FCSTD DOCUMENT  (FreeCAD 1.0R39319 (Git))
Label: ASSEMBLY-VSN1-LEFT
License: All rights reserved
LicenseURL: https://en.wikipedia.org/wiki/All_rights_reserved
objects: App::DocumentObjectGroup×3, App::Link×3, Sketcher::SketchObject×2, PartDesign::CoordinateSystem×1, App::FeaturePython×1, App::Part×1, PartDesign::Body×1
note: 6 computed .brp shape members not serialized (recipe doc carries the construction recipe); baked Part::Feature solids carry a one-line shape summary decoded from their .brp
EXTERNAL_REF file=ASSEMBLY-CANVAS.FCStd obj=LCS_Origin
EXTERNAL_REF file=ASSEMBLY-CANVAS.FCStd obj=Assembly
EXTERNAL_REF file=ASSEMBLY-VSN1-PCB-LEFT.FCStd obj=LCS_Origin
EXTERNAL_REF file=ASSEMBLY-VSN1-PCB-LEFT.FCStd obj=Assembly
EXTERNAL_REF file=ASSEMBLY-VSN1-FRONTPANEL-LEFT.FCStd obj=LCS_Origin
EXTERNAL_REF file=ASSEMBLY-VSN1-FRONTPANEL-LEFT.FCStd obj=Assembly

FEATURE [App::DocumentObjectGroup] Parts
FEATURE [PartDesign::CoordinateSystem] LCS_Origin
  AttacherType = Attacher::AttachEngine3D
  AttachmentSupport = -> [X_Axis]
  MapMode = 2
FEATURE [App::DocumentObjectGroup] Constraints
FEATURE [App::FeaturePython] Variables  # WARN: FeaturePython — macro-defined, semantics opaque (R4)
  Type = App::PropertyContainer
FEATURE [App::DocumentObjectGroup] Configurations
FEATURE [App::Link] ASSEMBLY_CANVAS_Assembly4  label="ASSEMBLY_CANVAS"
  AttachedBy = #LCS_Origin
  AttachedTo = Parent Assembly#LCS_Origin
  LinkedObject = -> <external ASSEMBLY-CANVAS.FCStd>#Assembly
  SolverId = Asm4EE
  expr: Placement = LCS_Origin.Placement * AttachmentOffset * ASSEMBLY_CANVAS#LCS_Origin.Placement ^ -1
FEATURE [App::Link] ASSEMBLY_VSN1_PCB_LEFT
  AttachedBy = #LCS_Origin
  AttachedTo = ASSEMBLY_CANVAS_Assembly4#LCS_Origin
  AttachmentOffset = pos=(0,0,-9.6) rot=(0,0,1;0rad)
  LinkPlacement = pos=(0,0,-9.6) rot=(0,0,1;0rad)
  LinkedObject = -> <external ASSEMBLY-VSN1-PCB-LEFT.FCStd>#Assembly
  Placement = pos=(0,0,-9.6) rot=(0,0,1;0rad)
  SolverId = Asm4EE
  expr: Placement = ASSEMBLY_CANVAS_Assembly4.Placement * ASSEMBLY_CANVAS#LCS_Origin.Placement * AttachmentOffset * ASSEMBLY_VSN1_PCB_LEFT#LCS_Origin.Placement ^ -1
FEATURE [App::Link] ASSEMBLY_VSN1_FRONTPANEL_LEFT
  AttachedBy = #LCS_Origin
  AttachedTo = ASSEMBLY_CANVAS_Assembly4#LCS_Origin
  AttachmentOffset = pos=(0,0,0.59) rot=(0,0,1;0rad)
  LinkPlacement = pos=(0,0,0.59) rot=(0,0,1;0rad)
  LinkedObject = -> <external ASSEMBLY-VSN1-FRONTPANEL-LEFT.FCStd>#Assembly
  Placement = pos=(0,0,0.59) rot=(0,0,1;0rad)
  SolverId = Asm4EE
  expr: Placement = ASSEMBLY_CANVAS_Assembly4.Placement * ASSEMBLY_CANVAS#LCS_Origin.Placement * AttachmentOffset * ASSEMBLY_VSN1_FRONTPANEL_LEFT#LCS_Origin.Placement ^ -1
FEATURE [Sketcher::SketchObject] Sketch_1
  ArcFitTolerance = 1e-06
  AttachmentSupport = -> [XZ_Plane]
  FullyConstrained = true
  MakeInternals = false
  MapMode = 5
  Placement = pos=(0,0,0) rot=(1,0,0;1.5708rad)
FEATURE [App::Part] Assembly
  AssemblyType = Part::Link
  Group = -> [LCS_Origin,Constraints,Variables,Configurations,ASSEMBLY_CANVAS_Assembly4,ASSEMBLY_VSN1_PCB_LEFT,ASSEMBLY_VSN1_FRONTPANEL_LEFT,Sketch_1]
  Origin = -> Origin
  Type = Assembly
FEATURE [Sketcher::SketchObject] Sketch
  ArcFitTolerance = 1e-06
  AttachmentOffset = pos=(0,0,26.67) rot=(0,0,1;0rad)
  AttachmentSupport = -> [XZ_Plane001]
  FullyConstrained = true
  MakeInternals = false
  MapMode = 5
  Placement = pos=(0,-26.67,5.9e-15) rot=(1,0,0;1.5708rad)
FEATURE [PartDesign::Body] Body
  AllowCompound = false
  Group = -> [Sketch]
  Origin = -> Origin001

RESOLVED EXTERNAL PARTS (link-assembly join: the EXTERNAL_REF files above that resolve inside this repo's crawl, each included once):
---- part ASSEMBLY-CANVAS.FCStd = doc fcstd_c2d832810578 ----
FCSTD DOCUMENT  (FreeCAD 1.0R39319 (Git))
Label: ASSEMBLY-CANVAS
License: All rights reserved
LicenseURL: https://en.wikipedia.org/wiki/All_rights_reserved
objects: App::Link×9, Part::FeaturePython×7, App::DocumentObjectGroup×3, PartDesign::CoordinateSystem×2, App::FeaturePython×1, Sketcher::SketchObject×1, App::Part×1
note: 11 computed .brp shape members not serialized (recipe doc carries the construction recipe); baked Part::Feature solids carry a one-line shape summary decoded from their .brp
EXTERNAL_REF file=../Design/PLASTIC-CANVAS/PLASTIC-CANVAS.FCStd obj=LCS_Origin
EXTERNAL_REF file=../Design/PLASTIC-CANVAS/PLASTIC-CANVAS.FCStd obj=Body002
EXTERNAL_REF file=../Design/PLASTIC-CANVAS/PLASTIC-CANVAS.FCStd obj=CircleAxis_1
EXTERNAL_REF file=../Design/RUBBER-FOOT/RUBBER-FOOT.FCStd obj=CircleAxis_2
EXTERNAL_REF file=../Design/RUBBER-FOOT/RUBBER-FOOT.FCStd obj=Body
EXTERNAL_REF file=../Design/INSERT-M1.6x2.5x3/INSERT-M1.6x2.5x3.FCStd obj=CircleAxis_1
EXTERNAL_REF file=../Design/PLASTIC-CANVAS/PLASTIC-CANVAS.FCStd obj=CircleAxis_3
EXTERNAL_REF file=../Design/INSERT-M1.6x2.5x3/INSERT-M1.6x2.5x3.FCStd obj=Body
EXTERNAL_REF file=../Design/INSERT-M1.6x2.5x4/INSERT-M1.6x2.5x4.FCStd obj=Plane_1
EXTERNAL_REF file=../Design/PLASTIC-CANVAS/PLASTIC-CANVAS.FCStd obj=CircleAxis_4
EXTERNAL_REF file=../Design/INSERT-M1.6x2.5x4/INSERT-M1.6x2.5x4.FCStd obj=Body
EXTERNAL_REF file=../Design/MAGNET-D3x14/MAGNET-D3x14.FCStd obj=LCS_1
EXTERNAL_REF file=../Design/PLASTIC-CANVAS/PLASTIC-CANVAS.FCStd obj=LCS_3
EXTERNAL_REF file=../Design/MAGNET-D3x14/MAGNET-D3x14.FCStd obj=Body001
EXTERNAL_REF file=../Design/PLASTIC-CANVAS/PLASTIC-CANVAS.FCStd obj=LCS_4
EXTERNAL_REF file=../Design/MAGNET-SQ3/MAGNET-SQ3.FCStd obj=Axis_2
EXTERNAL_REF file=../Design/PLASTIC-CANVAS/PLASTIC-CANVAS.FCStd obj=Axis_2
EXTERNAL_REF file=../Design/MAGNET-SQ3/MAGNET-SQ3.FCStd obj=Body002
EXTERNAL_REF file=PCBAs/PCBA-INTERFACE.FCStd obj=CircleAxis_1
EXTERNAL_REF file=../Design/PLASTIC-CANVAS/PLASTIC-CANVAS.FCStd obj=Axis_3
EXTERNAL_REF file=PCBAs/PCBA-INTERFACE.FCStd obj=PCBA_INTERFACE_3D_1
EXTERNAL_REF file=../Design/PLASTIC-CANVAS/PLASTIC-CANVAS.FCStd obj=LCS_5
EXTERNAL_REF file=../Design/PLASTIC-MAPMODE/PLASTIC-MAPMODE.FCStd obj=LCS_1
EXTERNAL_REF file=../Design/PLASTIC-MAPMODE/PLASTIC-MAPMODE.FCStd obj=Body

FEATURE [App::DocumentObjectGroup] Parts
FEATURE [PartDesign::CoordinateSystem] LCS_Origin
  AttacherType = Attacher::AttachEngine3D
  AttachmentSupport = -> [X_Axis]
  MapMode = 2
FEATURE [App::DocumentObjectGroup] Constraints
FEATURE [App::FeaturePython] Variables  # WARN: FeaturePython — macro-defined, semantics opaque (R4)
  Type = App::PropertyContainer
FEATURE [App::DocumentObjectGroup] Configurations
FEATURE [App::Link] PLASTIC_CANVAS  label="PLASTIC-CANVAS"
  AttachedBy = #LCS_Origin
  AttachedTo = Parent Assembly#LCS_Origin
  LinkedObject = -> <external ../Design/PLASTIC-CANVAS/PLASTIC-CANVAS.FCStd>#Body002
  SolverId = Asm4EE
  expr: Placement = LCS_Origin.Placement * AttachmentOffset * PLASTIC_CANVAS#LCS_Origin.Placement ^ -1
FEATURE [App::Link] RUBBER_FOOT  label="RUBBER-FOOT"
  AttachedBy = #CircleAxis_2
  AttachedTo = PLASTIC_CANVAS#CircleAxis_1
  LinkPlacement = pos=(-33.85,38,-16) rot=(0,0,1;0rad)
  LinkedObject = -> <external ../Design/RUBBER-FOOT/RUBBER-FOOT.FCStd>#Body
  Placement = pos=(-33.85,38,-16) rot=(0,0,1;0rad)
  SolverId = Asm4EE
  expr: Placement = PLASTIC_CANVAS.Placement * PLASTIC_CANVAS#CircleAxis_1.Placement * AttachmentOffset * RUBBER_FOOT#CircleAxis_2.Placement ^ -1
FEATURE [Part::FeaturePython] Circular_RUBBER_FOOT  label="Circular_RUBBER-FOOT"  # Draft array (typed FeaturePython)
  AngleStep = 90
  ArrayType = Circular Array
  Axis = -> LCS_Origin [Z]
  Count = 4
  Index = 1
  PlacementList = 4 placements: [(-33.85,38,-16),(-38,-33.85,-16),(33.85,-38,-16),(38,33.85,-16)]
  Placer = pos=(0,0,0) rot=(0,0,1;4.71239rad)
  ScaleList = (4) [(1,1,1),(1,1,1),(1,1,1),(1,1,1)]
  Scaler = 1
  ShowElement = false
  SourceObject = -> RUBBER_FOOT
  expr: .Placer.Rotation.Angle = AngleStep * Index
  expr: AngleStep = 360 / Count
FEATURE [App::Link] INSERT_M1_6x2_5x3  label="INSERT-M1.6x2.5x3"
  AttachedBy = #CircleAxis_1
  AttachedTo = PLASTIC_CANVAS#CircleAxis_3
  AttachmentOffset = pos=(0,0,0) rot=(1,0,0;3.14159rad)
  LinkPlacement = pos=(-26.67,26.67,-14) rot=(1,0,0;3.14159rad)
  LinkedObject = -> <external ../Design/INSERT-M1.6x2.5x3/INSERT-M1.6x2.5x3.FCStd>#Body
  Placement = pos=(-26.67,26.67,-14) rot=(1,0,0;3.14159rad)
  SolverId = Asm4EE
  expr: Placement = PLASTIC_CANVAS.Placement * PLASTIC_CANVAS#CircleAxis_3.Placement * AttachmentOffset * INSERT_M1_6x2_5x3#CircleAxis_1.Placement ^ -1
FEATURE [Part::FeaturePython] Circular_INSERT_M1_6x2_5x3  label="Circular_INSERT-M1.6x2.5x3"  # Draft array (typed FeaturePython)
  AngleStep = 90
  ArrayType = Circular Array
  Axis = -> LCS_Origin [Z]
  Count = 4
  Index = 1
  PlacementList = 4 placements: [(-26.67,26.67,-14),(-26.67,-26.67,-14),(26.67,-26.67,-14),(26.67,26.67,-14)]
  Placer = pos=(0,0,0) rot=(0,0,1;4.71239rad)
  ScaleList = (4) [(1,1,1),(1,1,1),(1,1,1),(1,1,1)]
  Scaler = 1
  ShowElement = false
  SourceObject = -> INSERT_M1_6x2_5x3
  expr: .Placer.Rotation.Angle = AngleStep * Index
  expr: AngleStep = 360 / Count
FEATURE [App::Link] INSERT_M1_6x2_5x4  label="INSERT-M1.6x2.5x4"
  AttachedBy = #Plane_1
  AttachedTo = PLASTIC_CANVAS#CircleAxis_4
  AttachmentOffset = pos=(0,0,0) rot=(1,0,0;3.14159rad)
  LinkPlacement = pos=(-50,50,-13.5) rot=(1,0,0;3.14159rad)
  LinkedObject = -> <external ../Design/INSERT-M1.6x2.5x4/INSERT-M1.6x2.5x4.FCStd>#Body
  Placement = pos=(-50,50,-13.5) rot=(1,0,0;3.14159rad)
  SolverId = Asm4EE
  expr: Placement = PLASTIC_CANVAS.Placement * PLASTIC_CANVAS#CircleAxis_4.Placement * AttachmentOffset * INSERT_M1_6x2_5x4#Plane_1.Placement ^ -1
FEATURE [Part::FeaturePython] Circular_INSERT_M1_6x2_5x4  label="Circular_INSERT-M1.6x2.5x4"  # Draft array (typed FeaturePython)
  AngleStep = 90
  ArrayType = Circular Array
  Axis = -> LCS_Origin [Z]
  Count = 4
  Index = 1
  PlacementList = 4 placements: [(-50,50,-13.5),(-50,-50,-13.5),(50,-50,-13.5),(50,50,-13.5)]
  Placer = pos=(0,0,0) rot=(0,0,1;4.71239rad)
  ScaleList = (4) [(1,1,1),(1,1,1),(1,1,1),(1,1,1)]
  Scaler = 1
  ShowElement = false
  SourceObject = -> INSERT_M1_6x2_5x4
  expr: .Placer.Rotation.Angle = AngleStep * Index
  expr: AngleStep = 360 / Count
FEATURE [App::Link] MAGNET_D3x14  label="MAGNET-D3x14"
  AttachedBy = #LCS_1
  AttachedTo = PLASTIC_CANVAS#LCS_3
  AttachmentOffset = pos=(0,0,0.25) rot=(0.71,-0.71,0;3.14159rad)
  LinkPlacement = pos=(-47,51.7,-13.25) rot=(0,0,-1;4.00114rad)
  LinkedObject = -> <external ../Design/MAGNET-D3x14/MAGNET-D3x14.FCStd>#Body001
  Placement = pos=(-47,51.7,-13.25) rot=(0,0,-1;4.00114rad)
  SolverId = Asm4EE
  expr: Placement = PLASTIC_CANVAS.Placement * PLASTIC_CANVAS#LCS_3.Placement * AttachmentOffset * MAGNET_D3x14#LCS_1.Placement ^ -1
FEATURE [App::Link] MAGNET_D3x015  label="MAGNET-D3x015"
  AttachedBy = #LCS_1
  AttachedTo = PLASTIC_CANVAS#LCS_4
  AttachmentOffset = pos=(0,0,0.25) rot=(1,0,0;3.14159rad)
  LinkPlacement = pos=(-51.7,47,-13.25) rot=(0,0,1;2.28204rad)
  LinkedObject = -> <external ../Design/MAGNET-D3x14/MAGNET-D3x14.FCStd>#Body001
  Placement = pos=(-51.7,47,-13.25) rot=(0,0,1;2.28204rad)
  SolverId = Asm4EE
  expr: Placement = PLASTIC_CANVAS.Placement * PLASTIC_CANVAS#LCS_4.Placement * AttachmentOffset * MAGNET_D3x14#LCS_1.Placement ^ -1
FEATURE [Part::FeaturePython] Circular_MAGNET_D3x14  label="Circular_MAGNET-D3x14"  # Draft array (typed FeaturePython)
  AngleStep = 90
  ArrayType = Circular Array
  Axis = -> LCS_Origin [Z]
  Count = 4
  Index = 1
  PlacementList = 4 placements: [(-47,51.7,-13.25),(-51.7,-47,-13.25),(47,-51.7,-13.25),(51.7,47,-13.25)]
  Placer = pos=(0,0,0) rot=(0,0,1;4.71239rad)
  ScaleList = (4) [(1,1,1),(1,1,1),(1,1,1),(1,1,1)]
  Scaler = 1
  ShowElement = false
  SourceObject = -> MAGNET_D3x14
  expr: .Placer.Rotation.Angle = AngleStep * Index
  expr: AngleStep = 360 / Count
FEATURE [Part::FeaturePython] Circular_MAGNET_D3x015  label="Circular_MAGNET-D3x015"  # Draft array (typed FeaturePython)
  AngleStep = 90
  ArrayType = Circular Array
  Axis = -> LCS_Origin [Z]
  Count = 4
  Index = 1
  PlacementList = 4 placements: [(-51.7,47,-13.25),(-47,-51.7,-13.25),(51.7,-47,-13.25),(47,51.7,-13.25)]
  Placer = pos=(0,0,0) rot=(0,0,1;4.71239rad)
  ScaleList = (4) [(1,1,1),(1,1,1),(1,1,1),(1,1,1)]
  Scaler = 1
  ShowElement = false
  SourceObject = -> MAGNET_D3x015
  expr: .Placer.Rotation.Angle = AngleStep * Index
  expr: AngleStep = 360 / Count
FEATURE [App::Link] MAGNET_SQ3  label="MAGNET-SQ3"
  AttachedBy = #Axis_2
  AttachedTo = PLASTIC_CANVAS#Axis_2
  AttachmentOffset = pos=(-0.2,0,16.18) rot=(0,1,0;3.14159rad)
  LinkPlacement = pos=(16.18,50.12,-13.25) rot=(0,0,1;3.14159rad)
  LinkedObject = -> <external ../Design/MAGNET-SQ3/MAGNET-SQ3.FCStd>#Body002
  Placement = pos=(16.18,50.12,-13.25) rot=(0,0,1;3.14159rad)
  SolverId = Asm4EE
  expr: Placement = PLASTIC_CANVAS.Placement * PLASTIC_CANVAS#Axis_2.Placement * AttachmentOffset * MAGNET_SQ3#Axis_2.Placement ^ -1
FEATURE [Part::FeaturePython] Circular_MAGNET_SQ3  label="Circular_MAGNET-SQ3"  # Draft array (typed FeaturePython)
  AngleStep = 90
  ArrayType = Circular Array
  Axis = -> LCS_Origin [Z]
  Count = 4
  Index = 1
  PlacementList = 4 placements: [(16.18,50.12,-13.25),(-50.12,16.18,-13.25),(-16.18,-50.12,-13.25),(50.12,-16.18,-13.25)]
  Placer = pos=(0,0,0) rot=(0,0,1;4.71239rad)
  ScaleList = (4) [(1,1,1),(1,1,1),(1,1,1),(1,1,1)]
  Scaler = 1
  ShowElement = false
  SourceObject = -> MAGNET_SQ3
  expr: .Placer.Rotation.Angle = AngleStep * Index
  expr: AngleStep = 360 / Count
FEATURE [App::Link] PCBA_INTERFACE_3D_1  label="PCBA-INTERFACE-3D 1"
  AttachedBy = #CircleAxis_1
  AttachedTo = PLASTIC_CANVAS#Axis_3
  AttachmentOffset = pos=(0,0,0) rot=(0,0,1.00409;4.71239rad)
  LinkPlacement = pos=(-100.032,53.1114,100.044) rot=(-1,0.000152,-0.000155;4.72984rad)
  LinkedObject = -> <external PCBAs/PCBA-INTERFACE.FCStd>#PCBA_INTERFACE_3D_1
  Placement = pos=(-100.032,53.1114,100.044) rot=(-1,0.000152,-0.000155;4.72984rad)
  SolverId = Asm4EE
  expr: Placement = PLASTIC_CANVAS.Placement * PLASTIC_CANVAS#Axis_3.Placement * AttachmentOffset * PCBA_INTERFACE#CircleAxis_1.Placement ^ -1
FEATURE [Part::FeaturePython] Circular_PCBA_INTERFACE_3D_1  label="Circular_PCBA-INTERFACE-3D 1"  # Draft array (typed FeaturePython)
  AngleStep = 90
  ArrayType = Circular Array
  Axis = -> LCS_Origin [Z]
  Count = 4
  Index = 1
  PlacementList = 4 placements: [(-100.032,53.1114,100.044),(-53.1114,-100.032,100.044),(100.032,-53.1114,100.044),(53.1114,100.032,100.044)]
  Placer = pos=(0,0,0) rot=(0,0,1;4.71239rad)
  ScaleList = (4) [(1,1,1),(1,1,1),(1,1,1),(1,1,1)]
  Scaler = 1
  ShowElement = false
  SourceObject = -> PCBA_INTERFACE_3D_1
  expr: .Placer.Rotation.Angle = AngleStep * Index
  expr: AngleStep = 360 / Count
FEATURE [PartDesign::CoordinateSystem] LCS_1
  AttacherType = Attacher::AttachEngine3D
FEATURE [Sketcher::SketchObject] Sketch_1
  ArcFitTolerance = 1e-06
  AttachmentSupport = -> [XZ_Plane]
  FullyConstrained = true
  MakeInternals = false
  MapMode = 5
  Placement = pos=(0,0,0) rot=(1,0,0;1.5708rad)
FEATURE [App::Link] PLASTIC_MAPMODE  label="PLASTIC-MAPMODE"
  AttachedBy = #LCS_1
  AttachedTo = PLASTIC_CANVAS#LCS_5
  AttachmentOffset = pos=(0,0,0.8) rot=(0,0,1;0rad)
  LinkPlacement = pos=(-2.147e-13,-48.5772,-6.3955) rot=(-0.579059,-0.573917,-0.579059;4.18363rad)
  LinkedObject = -> <external ../Design/PLASTIC-MAPMODE/PLASTIC-MAPMODE.FCStd>#Body
  Placement = pos=(-2.147e-13,-48.5772,-6.3955) rot=(-0.579059,-0.573917,-0.579059;4.18363rad)
  SolverId = Asm4EE
  expr: Placement = PLASTIC_CANVAS.Placement * PLASTIC_CANVAS#LCS_5.Placement * AttachmentOffset * PLASTIC_MAPMODE#LCS_1.Placement ^ -1
FEATURE [App::Part] Assembly
  AssemblyType = Part::Link
  Group = -> [LCS_Origin,Constraints,Variables,Configurations,PLASTIC_CANVAS,RUBBER_FOOT,Circular_RUBBER_FOOT,INSERT_M1_6x2_5x3,Circular_INSERT_M1_6x2_5x3,INSERT_M1_6x2_5x4,Circular_INSERT_M1_6x2_5x4,MAGNET_D3x14,MAGNET_D3x015,Circular_MAGNET_D3x14,Circular_MAGNET_D3x015,MAGNET_SQ3,Circular_MAGNET_SQ3,PCBA_INTERFACE_3D_1,Circular_PCBA_INTERFACE_3D_1,LCS_1,Sketch_1,PLASTIC_MAPMODE]
  Origin = -> Origin
  Type = Assembly
---- part ASSEMBLY-VSN1-FRONTPANEL-LEFT.FCStd = doc fcstd_67dcef270430 ----
FCSTD DOCUMENT  (FreeCAD 1.0R39319 (Git))
Label: ASSEMBLY-VSN1-FRONTPANEL-LEFT
License: All rights reserved
LicenseURL: https://en.wikipedia.org/wiki/All_rights_reserved
objects: App::Link×10, App::DocumentObjectGroup×3, PartDesign::CoordinateSystem×1, App::FeaturePython×1, App::Part×1
note: 1 computed .brp shape members not serialized (recipe doc carries the construction recipe); baked Part::Feature solids carry a one-line shape summary decoded from their .brp
EXTERNAL_REF file=Frontpanels/FRONTPANEL-VSN1-L.FCStd obj=LCS_1
EXTERNAL_REF file=Frontpanels/FRONTPANEL-VSN1-L.FCStd obj=Body001
EXTERNAL_REF file=../Design/PLASTIC-LIGHTPIPE/PLASTIC-LIGHTPIPE.FCStd obj=LCS_1
EXTERNAL_REF file=../Design/PLASTIC-LIGHTPIPE/PLASTIC-LIGHTPIPE.FCStd obj=Body
EXTERNAL_REF file=../Design/SCREW-M1.6x16/SCREW-M1.6x16.FCStd obj=LCS_1
EXTERNAL_REF file=../Design/SCREW-M1.6x16/SCREW-M1.6x16.FCStd obj=Body

FEATURE [App::DocumentObjectGroup] Parts
FEATURE [PartDesign::CoordinateSystem] LCS_Origin
  AttacherType = Attacher::AttachEngine3D
  AttachmentSupport = -> [X_Axis]
  MapMode = 2
FEATURE [App::DocumentObjectGroup] Constraints
FEATURE [App::FeaturePython] Variables  # WARN: FeaturePython — macro-defined, semantics opaque (R4)
  Type = App::PropertyContainer
FEATURE [App::DocumentObjectGroup] Configurations
FEATURE [App::Link] FP_VSN1_L_3D_1  label="FP-VSN1-L-3D 1"
  AttachedBy = #LCS_1
  AttachedTo = Parent Assembly#LCS_Origin
  LinkedObject = -> <external Frontpanels/FRONTPANEL-VSN1-L.FCStd>#Body001
  SolverId = Asm4EE
  expr: Placement = LCS_Origin.Placement * AttachmentOffset * FRONTPANEL_VSN1_L#LCS_1.Placement ^ -1
FEATURE [App::Link] PLASTIC_LIGHTPIPE  label="PLASTIC-LIGHTPIPE"
  AttachedBy = #LCS_1
  AttachedTo = FP_VSN1_L_3D_1#CircleAxis_1
  AttachmentOffset = pos=(0,0,0) rot=(1,0,0;3.14159rad)
  LinkPlacement = pos=(5.82492,36.3902,0.91) rot=(0,0,1;4.71239rad)
  LinkedObject = -> <external ../Design/PLASTIC-LIGHTPIPE/PLASTIC-LIGHTPIPE.FCStd>#Body
  Placement = pos=(5.82492,36.3902,0.91) rot=(0,0,1;4.71239rad)
  SolverId = Asm4EE
  expr: Placement = FP_VSN1_L_3D_1.Placement * FRONTPANEL_VSN1_L#CircleAxis_1.Placement * AttachmentOffset * PLASTIC_LIGHTPIPE#LCS_1.Placement ^ -1
FEATURE [App::Link] PLASTIC_LIGHTPIPE001  label="PLASTIC-LIGHTPIPE001"
  AttachedBy = #LCS_1
  AttachedTo = FP_VSN1_L_3D_1#CircleAxis_2
  AttachmentOffset = pos=(0,0,0) rot=(1,0,0;3.14159rad)
  LinkPlacement = pos=(7.8295,39.8623,0.91) rot=(0,0,1;4.71239rad)
  LinkedObject = -> <external ../Design/PLASTIC-LIGHTPIPE/PLASTIC-LIGHTPIPE.FCStd>#Body
  Placement = pos=(7.8295,39.8623,0.91) rot=(0,0,1;4.71239rad)
  SolverId = Asm4EE
  expr: Placement = FP_VSN1_L_3D_1.Placement * FRONTPANEL_VSN1_L#CircleAxis_2.Placement * AttachmentOffset * PLASTIC_LIGHTPIPE#LCS_1.Placement ^ -1
FEATURE [App::Link] PLASTIC_LIGHTPIPE002  label="PLASTIC-LIGHTPIPE002"
  AttachedBy = #LCS_1
  AttachedTo = FP_VSN1_L_3D_1#CircleAxis_3
  AttachmentOffset = pos=(0,0,0) rot=(1,0,0;3.14159rad)
  LinkPlacement = pos=(10.4065,42.9335,0.91) rot=(0,0,1;4.71239rad)
  LinkedObject = -> <external ../Design/PLASTIC-LIGHTPIPE/PLASTIC-LIGHTPIPE.FCStd>#Body
  Placement = pos=(10.4065,42.9335,0.91) rot=(0,0,1;4.71239rad)
  SolverId = Asm4EE
  expr: Placement = FP_VSN1_L_3D_1.Placement * FRONTPANEL_VSN1_L#CircleAxis_3.Placement * AttachmentOffset * PLASTIC_LIGHTPIPE#LCS_1.Placement ^ -1
FEATURE [App::Link] PLASTIC_LIGHTPIPE003  label="PLASTIC-LIGHTPIPE003"
  AttachedBy = #LCS_1
  AttachedTo = FP_VSN1_L_3D_1#CircleAxis_4
  AttachmentOffset = pos=(0,0,0) rot=(1,0,0;3.14159rad)
  LinkPlacement = pos=(13.4777,45.5105,0.91) rot=(0,0,1;4.71239rad)
  LinkedObject = -> <external ../Design/PLASTIC-LIGHTPIPE/PLASTIC-LIGHTPIPE.FCStd>#Body
  Placement = pos=(13.4777,45.5105,0.91) rot=(0,0,1;4.71239rad)
  SolverId = Asm4EE
  expr: Placement = FP_VSN1_L_3D_1.Placement * FRONTPANEL_VSN1_L#CircleAxis_4.Placement * AttachmentOffset * PLASTIC_LIGHTPIPE#LCS_1.Placement ^ -1
FEATURE [App::Link] PLASTIC_LIGHTPIPE004  label="PLASTIC-LIGHTPIPE004"
  AttachedBy = #LCS_1
  AttachedTo = FP_VSN1_L_3D_1#CircleAxis_5
  AttachmentOffset = pos=(0,0,0) rot=(1,0,0;3.14159rad)
  LinkPlacement = pos=(16.9498,47.5151,0.91) rot=(0,0,1;4.71239rad)
  LinkedObject = -> <external ../Design/PLASTIC-LIGHTPIPE/PLASTIC-LIGHTPIPE.FCStd>#Body
  Placement = pos=(16.9498,47.5151,0.91) rot=(0,0,1;4.71239rad)
  SolverId = Asm4EE
  expr: Placement = FP_VSN1_L_3D_1.Placement * FRONTPANEL_VSN1_L#CircleAxis_5.Placement * AttachmentOffset * PLASTIC_LIGHTPIPE#LCS_1.Placement ^ -1
FEATURE [App::Link] SCREW_M1_6x16  label="SCREW-M1.6x16"
  AttachedBy = #LCS_1
  AttachedTo = FP_VSN1_L_3D_1#CircleAxis_6
  LinkPlacement = pos=(-50,50,0.91) rot=(0,0,1;0rad)
  LinkedObject = -> <external ../Design/SCREW-M1.6x16/SCREW-M1.6x16.FCStd>#Body
  Placement = pos=(-50,50,0.91) rot=(0,0,1;0rad)
  SolverId = Asm4EE
  expr: Placement = FP_VSN1_L_3D_1.Placement * FRONTPANEL_VSN1_L#CircleAxis_6.Placement * AttachmentOffset * SCREW_M1_6x16#LCS_1.Placement ^ -1
FEATURE [App::Link] SCREW_M1_6x017  label="SCREW-M1.6x017"
  AttachedBy = #LCS_1
  AttachedTo = FP_VSN1_L_3D_1#CircleAxis_7
  LinkPlacement = pos=(50,50,0.91) rot=(0,0,1;0rad)
  LinkedObject = -> <external ../Design/SCREW-M1.6x16/SCREW-M1.6x16.FCStd>#Body
  Placement = pos=(50,50,0.91) rot=(0,0,1;0rad)
  SolverId = Asm4EE
  expr: Placement = FP_VSN1_L_3D_1.Placement * FRONTPANEL_VSN1_L#CircleAxis_7.Placement * AttachmentOffset * SCREW_M1_6x16#LCS_1.Placement ^ -1
FEATURE [App::Link] SCREW_M1_6x018  label="SCREW-M1.6x018"
  AttachedBy = #LCS_1
  AttachedTo = FP_VSN1_L_3D_1#CircleAxis_8
  LinkPlacement = pos=(50,-50,0.91) rot=(0,0,1;0rad)
  LinkedObject = -> <external ../Design/SCREW-M1.6x16/SCREW-M1.6x16.FCStd>#Body
  Placement = pos=(50,-50,0.91) rot=(0,0,1;0rad)
  SolverId = Asm4EE
  expr: Placement = FP_VSN1_L_3D_1.Placement * FRONTPANEL_VSN1_L#CircleAxis_8.Placement * AttachmentOffset * SCREW_M1_6x16#LCS_1.Placement ^ -1
FEATURE [App::Link] SCREW_M1_6x019  label="SCREW-M1.6x019"
  AttachedBy = #LCS_1
  AttachedTo = FP_VSN1_L_3D_1#CircleAxis_9
  LinkPlacement = pos=(-50,-50,0.91) rot=(0,0,1;0rad)
  LinkedObject = -> <external ../Design/SCREW-M1.6x16/SCREW-M1.6x16.FCStd>#Body
  Placement = pos=(-50,-50,0.91) rot=(0,0,1;0rad)
  SolverId = Asm4EE
  expr: Placement = FP_VSN1_L_3D_1.Placement * FRONTPANEL_VSN1_L#CircleAxis_9.Placement * AttachmentOffset * SCREW_M1_6x16#LCS_1.Placement ^ -1
FEATURE [App::Part] Assembly
  AssemblyType = Part::Link
  Group = -> [LCS_Origin,Constraints,Variables,Configurations,FP_VSN1_L_3D_1,PLASTIC_LIGHTPIPE,PLASTIC_LIGHTPIPE001,PLASTIC_LIGHTPIPE002,PLASTIC_LIGHTPIPE003,PLASTIC_LIGHTPIPE004,SCREW_M1_6x16,SCREW_M1_6x017,SCREW_M1_6x018,SCREW_M1_6x019]
  Origin = -> Origin
  Type = Assembly
---- part ASSEMBLY-VSN1-PCB-LEFT.FCStd = doc fcstd_23929182a272 ----
FCSTD DOCUMENT  (FreeCAD 1.0R39319 (Git))
Label: ASSEMBLY-VSN1-PCB-LEFT
License: All rights reserved
LicenseURL: https://en.wikipedia.org/wiki/All_rights_reserved
objects: App::Link×24, Part::FeaturePython×4, App::DocumentObjectGroup×3, PartDesign::CoordinateSystem×1, App::FeaturePython×1, App::Part×1
note: 5 computed .brp shape members not serialized (recipe doc carries the construction recipe); baked Part::Feature solids carry a one-line shape summary decoded from their .brp
EXTERNAL_REF file=PCBAs/PCBA-VSNX.FCStd obj=LCS_1
EXTERNAL_REF file=PCBAs/PCBA-VSNX.FCStd obj=PCBA_VSNX_3D_1
EXTERNAL_REF file=PCBAs/PCBA-VSNX.FCStd obj=Plane_2
EXTERNAL_REF file=PCBAs/PCBA-VSNX-SPACER.FCStd obj=Plane_Bottom_1
EXTERNAL_REF file=PCBAs/PCBA-VSNX-SPACER.FCStd obj=PCBA_VSNX_SPACER_3D_1
EXTERNAL_REF file=PCBAs/PCBA-VSNX-SPACER.FCStd obj=Plane_Top_1
EXTERNAL_REF file=PCBAs/PCBA-VSNX-LCDMOUNT-LEFT.FCStd obj=Plane_1
EXTERNAL_REF file=PCBAs/PCBA-VSNX-LCDMOUNT-LEFT.FCStd obj=PCBA_VSNX_LCDMOUNT_3D_1
EXTERNAL_REF file=PCBAs/PCBA-VSNX.FCStd obj=Axis_3
EXTERNAL_REF file=../Design/THT-ENDLESSPOT/THT-ENDLESSPOT.FCStd obj=Axis_1
EXTERNAL_REF file=../Design/THT-ENDLESSPOT/THT-ENDLESSPOT.FCStd obj=Body
EXTERNAL_REF file=PCBAs/PCBA-VSNX-LCDMOUNT-LEFT.FCStd obj=CircleAxis_1
EXTERNAL_REF file=../Design/SCREW-M1.6x5-C/SCREW-M1.6x5-C.FCStd obj=CircleAxis_1
EXTERNAL_REF file=../Design/SCREW-M1.6x5-C/SCREW-M1.6x5-C.FCStd obj=Body
EXTERNAL_REF file=PCBAs/PCBA-VSNX-LCDMOUNT-LEFT.FCStd obj=CircleAxis_2
EXTERNAL_REF file=PCBAs/PCBA-VSNX-LCDMOUNT-LEFT.FCStd obj=CircleAxis_3
EXTERNAL_REF file=PCBAs/PCBA-VSNX-LCDMOUNT-LEFT.FCStd obj=CircleAxis_4
EXTERNAL_REF file=PCBAs/PCBA-VSNX-LCDMOUNT-LEFT.FCStd obj=CircleAxis_5
EXTERNAL_REF file=PCBAs/PCBA-VSNX-LCDMOUNT-LEFT.FCStd obj=CircleAxis_6
EXTERNAL_REF file=PCBAs/PCBA-VSNX-LCDMOUNT-LEFT.FCStd obj=CircleAxis_7
EXTERNAL_REF file=PCBAs/PCBA-VSNX-LCDMOUNT-LEFT.FCStd obj=CircleAxis_8
EXTERNAL_REF file=../Design/PLASTIC-VSN1-DISPLAY-INTERFACE/PLASTIC-VSN1-DISPLAY-INTERFACE.FCStd obj=LCS_1
EXTERNAL_REF file=../Design/PLASTIC-VSN1-DISPLAY-INTERFACE/PLASTIC-VSN1-DISPLAY-INTERFACE.FCStd obj=Body
EXTERNAL_REF file=PCBAs/PCBA-VSNX.FCStd obj=LCS_2
EXTERNAL_REF file=../Design/PLASTIC-VSN1-BUTTON/PLASTIC-VSN1-BUTTON.FCStd obj=LCS_1
EXTERNAL_REF file=../Design/PLASTIC-VSN1-BUTTON/PLASTIC-VSN1-BUTTON.FCStd obj=Body001
EXTERNAL_REF file=PCBAs/PCBA-VSNX-LCDMOUNT-LEFT.FCStd obj=LCS_2
EXTERNAL_REF file=../Design/THT-HALL-SWITCH/THT-HALL-SWITCH.FCStd obj=LCS_Origin
EXTERNAL_REF file=../Design/THT-HALL-SWITCH/THT-HALL-SWITCH.FCStd obj=Body
EXTERNAL_REF file=../Design/PLASTIC-LOW-PROFILE-KEYCAP/PLASTIC-LOW-PROFILE-KEYCAP_THT.FCStd obj=LCS_1
EXTERNAL_REF file=../Design/THT-HALL-SWITCH/THT-HALL-SWITCH.FCStd obj=LCS_1
EXTERNAL_REF file=../Design/PLASTIC-LOW-PROFILE-KEYCAP/PLASTIC-LOW-PROFILE-KEYCAP_THT.FCStd obj=Body
EXTERNAL_REF file=PCBAs/PCBA-VSNX.FCStd obj=LCS_3
EXTERNAL_REF file=../Design/SPACER/SPACER.FCStd obj=LCS_1
EXTERNAL_REF file=../Design/SPACER/SPACER.FCStd obj=Body004
EXTERNAL_REF file=PCBAs/PCBA-VSNX.FCStd obj=LCS_4
EXTERNAL_REF file=../Design/SCREW-M1.6x8/SCREW-M1.6x8.FCStd obj=LCS_1
EXTERNAL_REF file=../Design/SPACER/SPACER.FCStd obj=LCS_2
EXTERNAL_REF file=../Design/SCREW-M1.6x8/SCREW-M1.6x8.FCStd obj=Body
EXTERNAL_REF file=../Design/PLASTIC-TEK2-KNOB-INTERFACE/PLASTIC-TEK2-KNOB-INTERFACE.FCStd obj=LCS_2
EXTERNAL_REF file=../Design/THT-ENDLESSPOT/THT-ENDLESSPOT.FCStd obj=LCS_2
EXTERNAL_REF file=../Design/PLASTIC-TEK2-KNOB-INTERFACE/PLASTIC-TEK2-KNOB-INTERFACE.FCStd obj=Body
EXTERNAL_REF file=../Design/KNOB-TEK2/KNOB-TEK2.FCStd obj=LCS_1
EXTERNAL_REF file=../Design/PLASTIC-TEK2-KNOB-INTERFACE/PLASTIC-TEK2-KNOB-INTERFACE.FCStd obj=LCS_1
EXTERNAL_REF file=../Design/KNOB-TEK2/KNOB-TEK2.FCStd obj=Body
EXTERNAL_REF file=../Design/PLASTIC-VSN1-DISPLAY-INTERFACE/PLASTIC-VSN1-DISPLAY-INTERFACE_merged_left.FCStd obj=LCS_2
EXTERNAL_REF file=../Design/PLASTIC-VSN1-DISPLAY-INTERFACE/PLASTIC-VSN1-DISPLAY-INTERFACE_merged_left.FCStd obj=Body

FEATURE [App::DocumentObjectGroup] Parts
FEATURE [PartDesign::CoordinateSystem] LCS_Origin
  AttacherType = Attacher::AttachEngine3D
  AttachmentSupport = -> [X_Axis]
  MapMode = 2
FEATURE [App::DocumentObjectGroup] Constraints
FEATURE [App::FeaturePython] Variables  # WARN: FeaturePython — macro-defined, semantics opaque (R4)
  Type = App::PropertyContainer
FEATURE [App::DocumentObjectGroup] Configurations
FEATURE [App::Link] PCBA_VSNX_3D_1  label="PCBA-VSNX-3D 1"
  AttachedBy = #LCS_1
  AttachedTo = Parent Assembly#LCS_Origin
  LinkedObject = -> <external PCBAs/PCBA-VSNX.FCStd>#PCBA_VSNX_3D_1
  SolverId = Asm4EE
  expr: Placement = LCS_Origin.Placement * AttachmentOffset * PCBA_VSNX#LCS_1.Placement ^ -1
FEATURE [App::Link] PCBA_VSNX_SPACER_3D_1  label="PCBA-VSNX-SPACER-3D 1"
  AttachedBy = #Plane_Bottom_1
  AttachedTo = PCBA_VSNX_3D_1#Plane_2
  AttachmentOffset = pos=(0,0,0) rot=(1,0,0;3.14159rad)
  LinkPlacement = pos=(0,0,1.51) rot=(0,0,1;0rad)
  LinkedObject = -> <external PCBAs/PCBA-VSNX-SPACER.FCStd>#PCBA_VSNX_SPACER_3D_1
  Placement = pos=(0,0,1.51) rot=(0,0,1;0rad)
  SolverId = Asm4EE
  expr: Placement = PCBA_VSNX_3D_1.Placement * PCBA_VSNX#Plane_2.Placement * AttachmentOffset * PCBA_VSNX_SPACER#Plane_Bottom_1.Placement ^ -1
FEATURE [App::Link] PCBA_VSNX_SPACER_3D_002  label="PCBA-VSNX-SPACER-3D 002"
  AttachedBy = #Plane_Bottom_1
  AttachedTo = PCBA_VSNX_SPACER_3D_1#Plane_Top_1
  AttachmentOffset = pos=(0,0,0) rot=(1,0,0;3.14159rad)
  LinkPlacement = pos=(0,0,2.62) rot=(0,0,1;0rad)
  LinkedObject = -> <external PCBAs/PCBA-VSNX-SPACER.FCStd>#PCBA_VSNX_SPACER_3D_1
  Placement = pos=(0,0,2.62) rot=(0,0,1;0rad)
  SolverId = Asm4EE
  expr: Placement = PCBA_VSNX_SPACER_3D_1.Placement * PCBA_VSNX_SPACER#Plane_Top_1.Placement * AttachmentOffset * PCBA_VSNX_SPACER#Plane_Bottom_1.Placement ^ -1
FEATURE [App::Link] PCBA_VSNX_LCDMOUNT_3D_1  label="PCBA-VSNX-LCDMOUNT-3D 1"
  AttachedBy = #Plane_1
  AttachedTo = PCBA_VSNX_SPACER_3D_002#Plane_Top_1
  AttachmentOffset = pos=(0,0,0) rot=(1,0,0;3.14159rad)
  LinkPlacement = pos=(0,0,3.73) rot=(0,0,1;0rad)
  LinkedObject = -> <external PCBAs/PCBA-VSNX-LCDMOUNT-LEFT.FCStd>#PCBA_VSNX_LCDMOUNT_3D_1
  Placement = pos=(0,0,3.73) rot=(0,0,1;0rad)
  SolverId = Asm4EE
  expr: Placement = PCBA_VSNX_SPACER_3D_002.Placement * PCBA_VSNX_SPACER#Plane_Top_1.Placement * AttachmentOffset * PCBA_VSNX_LCDMOUNT_LEFT#Plane_1.Placement ^ -1
FEATURE [App::Link] THT_ENDLESSPOT  label="THT-ENDLESSPOT"
  AttachedBy = #Axis_1
  AttachedTo = PCBA_VSNX_3D_1#Axis_3
  AttachmentOffset = pos=(0,0,-25) rot=(0,-1,0;3.14159rad)
  LinkPlacement = pos=(26.6653,26.6675,1.50877) rot=(0,0,1;4.71239rad)
  LinkedObject = -> <external ../Design/THT-ENDLESSPOT/THT-ENDLESSPOT.FCStd>#Body
  Placement = pos=(26.6653,26.6675,1.50877) rot=(0,0,1;4.71239rad)
  SolverId = Asm4EE
  expr: Placement = PCBA_VSNX_3D_1.Placement * PCBA_VSNX#Axis_3.Placement * AttachmentOffset * THT_ENDLESSPOT#Axis_1.Placement ^ -1
FEATURE [App::Link] SCREW_M1_6x5_C  label="SCREW-M1.6x5-C"
  AttachedBy = #CircleAxis_1
  AttachedTo = PCBA_VSNX_LCDMOUNT_3D_1#CircleAxis_1
  AttachmentOffset = pos=(0,0,0) rot=(1,0,0;3.14159rad)
  LinkPlacement = pos=(-25.8762,-12.9381,4.04) rot=(0,0,1;1.5708rad)
  LinkedObject = -> <external ../Design/SCREW-M1.6x5-C/SCREW-M1.6x5-C.FCStd>#Body
  Placement = pos=(-25.8762,-12.9381,4.04) rot=(0,0,1;1.5708rad)
  SolverId = Asm4EE
  expr: Placement = PCBA_VSNX_LCDMOUNT_3D_1.Placement * PCBA_VSNX_LCDMOUNT_LEFT#CircleAxis_1.Placement * AttachmentOffset * SCREW_M1_6x5_C#CircleAxis_1.Placement ^ -1
FEATURE [App::Link] SCREW_M1_6x5_C001  label="SCREW-M1.6x5-C001"
  AttachedBy = #CircleAxis_1
  AttachedTo = PCBA_VSNX_LCDMOUNT_3D_1#CircleAxis_2
  AttachmentOffset = pos=(0,0,0) rot=(1,0,0;3.14159rad)
  LinkPlacement = pos=(-25.8762,-38.8144,4.04) rot=(0,0,1;1.5708rad)
  LinkedObject = -> <external ../Design/SCREW-M1.6x5-C/SCREW-M1.6x5-C.FCStd>#Body
  Placement = pos=(-25.8762,-38.8144,4.04) rot=(0,0,1;1.5708rad)
  SolverId = Asm4EE
  expr: Placement = PCBA_VSNX_LCDMOUNT_3D_1.Placement * PCBA_VSNX_LCDMOUNT_LEFT#CircleAxis_2.Placement * AttachmentOffset * SCREW_M1_6x5_C#CircleAxis_1.Placement ^ -1
FEATURE [App::Link] SCREW_M1_6x5_C002  label="SCREW-M1.6x5-C002"
  AttachedBy = #CircleAxis_1
  AttachedTo = PCBA_VSNX_LCDMOUNT_3D_1#CircleAxis_3
  AttachmentOffset = pos=(0,0,0) rot=(1,0,0;3.14159rad)
  LinkPlacement = pos=(25.8762,-12.9381,4.04) rot=(0,0,1;1.5708rad)
  LinkedObject = -> <external ../Design/SCREW-M1.6x5-C/SCREW-M1.6x5-C.FCStd>#Body
  Placement = pos=(25.8762,-12.9381,4.04) rot=(0,0,1;1.5708rad)
  SolverId = Asm4EE
  expr: Placement = PCBA_VSNX_LCDMOUNT_3D_1.Placement * PCBA_VSNX_LCDMOUNT_LEFT#CircleAxis_3.Placement * AttachmentOffset * SCREW_M1_6x5_C#CircleAxis_1.Placement ^ -1
FEATURE [App::Link] SCREW_M1_6x5_C003  label="SCREW-M1.6x5-C003"
  AttachedBy = #CircleAxis_1
  AttachedTo = PCBA_VSNX_LCDMOUNT_3D_1#CircleAxis_4
  AttachmentOffset = pos=(0,0,0) rot=(1,0,0;3.14159rad)
  LinkPlacement = pos=(25.8762,-38.8144,4.04) rot=(0,0,1;1.5708rad)
  LinkedObject = -> <external ../Design/SCREW-M1.6x5-C/SCREW-M1.6x5-C.FCStd>#Body
  Placement = pos=(25.8762,-38.8144,4.04) rot=(0,0,1;1.5708rad)
  SolverId = Asm4EE
  expr: Placement = PCBA_VSNX_LCDMOUNT_3D_1.Placement * PCBA_VSNX_LCDMOUNT_LEFT#CircleAxis_4.Placement * AttachmentOffset * SCREW_M1_6x5_C#CircleAxis_1.Placement ^ -1
FEATURE [App::Link] SCREW_M1_6x5_C004  label="SCREW-M1.6x5-C004"
  AttachedBy = #CircleAxis_1
  AttachedTo = PCBA_VSNX_LCDMOUNT_3D_1#CircleAxis_5
  AttachmentOffset = pos=(0,0,0) rot=(1,0,0;3.14159rad)
  LinkPlacement = pos=(38.17,36.67,4.04) rot=(0,0,1;1.5708rad)
  LinkedObject = -> <external ../Design/SCREW-M1.6x5-C/SCREW-M1.6x5-C.FCStd>#Body
  Placement = pos=(38.17,36.67,4.04) rot=(0,0,1;1.5708rad)
  SolverId = Asm4EE
  expr: Placement = PCBA_VSNX_LCDMOUNT_3D_1.Placement * PCBA_VSNX_LCDMOUNT_LEFT#CircleAxis_5.Placement * AttachmentOffset * SCREW_M1_6x5_C#CircleAxis_1.Placement ^ -1
FEATURE [App::Link] SCREW_M1_6x5_C005  label="SCREW-M1.6x5-C005"
  AttachedBy = #CircleAxis_1
  AttachedTo = PCBA_VSNX_LCDMOUNT_3D_1#CircleAxis_6
  AttachmentOffset = pos=(0,0,0) rot=(1,0,0;3.14159rad)
  LinkPlacement = pos=(38.17,16.67,4.04) rot=(0,0,1;1.5708rad)
  LinkedObject = -> <external ../Design/SCREW-M1.6x5-C/SCREW-M1.6x5-C.FCStd>#Body
  Placement = pos=(38.17,16.67,4.04) rot=(0,0,1;1.5708rad)
  SolverId = Asm4EE
  expr: Placement = PCBA_VSNX_LCDMOUNT_3D_1.Placement * PCBA_VSNX_LCDMOUNT_LEFT#CircleAxis_6.Placement * AttachmentOffset * SCREW_M1_6x5_C#CircleAxis_1.Placement ^ -1
FEATURE [App::Link] SCREW_M1_6x5_C006  label="SCREW-M1.6x5-C006"
  AttachedBy = #CircleAxis_1
  AttachedTo = PCBA_VSNX_LCDMOUNT_3D_1#CircleAxis_7
  AttachmentOffset = pos=(0,0,0) rot=(1,0,0;3.14159rad)
  LinkPlacement = pos=(-38.17,16.67,4.04) rot=(0,0,1;1.5708rad)
  LinkedObject = -> <external ../Design/SCREW-M1.6x5-C/SCREW-M1.6x5-C.FCStd>#Body
  Placement = pos=(-38.17,16.67,4.04) rot=(0,0,1;1.5708rad)
  SolverId = Asm4EE
  expr: Placement = PCBA_VSNX_LCDMOUNT_3D_1.Placement * PCBA_VSNX_LCDMOUNT_LEFT#CircleAxis_7.Placement * AttachmentOffset * SCREW_M1_6x5_C#CircleAxis_1.Placement ^ -1
FEATURE [App::Link] SCREW_M1_6x5_C007  label="SCREW-M1.6x5-C007"
  AttachedBy = #CircleAxis_1
  AttachedTo = PCBA_VSNX_LCDMOUNT_3D_1#CircleAxis_8
  AttachmentOffset = pos=(0,0,0) rot=(1,0,0;3.14159rad)
  LinkPlacement = pos=(-38.17,36.67,4.04) rot=(0,0,1;1.5708rad)
  LinkedObject = -> <external ../Design/SCREW-M1.6x5-C/SCREW-M1.6x5-C.FCStd>#Body
  Placement = pos=(-38.17,36.67,4.04) rot=(0,0,1;1.5708rad)
  SolverId = Asm4EE
  expr: Placement = PCBA_VSNX_LCDMOUNT_3D_1.Placement * PCBA_VSNX_LCDMOUNT_LEFT#CircleAxis_8.Placement * AttachmentOffset * SCREW_M1_6x5_C#CircleAxis_1.Placement ^ -1
FEATURE [App::Link] PLASTIC_VSN1_DISPLAY_INTERFACE  label="PLASTIC-VSN1-DISPLAY-INTERFACE"
  AttachedBy = #LCS_1
  AttachedTo = PCBA_VSNX_LCDMOUNT_3D_1#LCS_1
  LinkPlacement = pos=(-26.67,26.67,8.775) rot=(0,0,1;0rad)
  LinkedObject = -> <external ../Design/PLASTIC-VSN1-DISPLAY-INTERFACE/PLASTIC-VSN1-DISPLAY-INTERFACE.FCStd>#Body
  Placement = pos=(-26.67,26.67,8.775) rot=(0,0,1;0rad)
  SolverId = Asm4EE
  expr: Placement = PCBA_VSNX_LCDMOUNT_3D_1.Placement * PCBA_VSNX_LCDMOUNT_LEFT#LCS_1.Placement * AttachmentOffset * PLASTIC_VSN1_DISPLAY_INTERFACE#LCS_1.Placement ^ -1
FEATURE [App::Link] PLASTIC_VSN1_BUTTON  label="PLASTIC-VSN1-BUTTON"
  AttachedBy = #LCS_1
  AttachedTo = PCBA_VSNX_3D_1#LCS_2
  AttachmentOffset = pos=(0,0,0) rot=(0,0,1;4.71239rad)
  LinkPlacement = pos=(-41.67,4.67,1.095) rot=(0,0,1;0rad)
  LinkedObject = -> <external ../Design/PLASTIC-VSN1-BUTTON/PLASTIC-VSN1-BUTTON.FCStd>#Body001
  Placement = pos=(-41.67,4.67,1.095) rot=(0,0,1;0rad)
  SolverId = Asm4EE
  expr: Placement = PCBA_VSNX_3D_1.Placement * PCBA_VSNX#LCS_2.Placement * AttachmentOffset * PLASTIC_VSN1_BUTTON#LCS_1.Placement ^ -1
FEATURE [App::Link] Body  label="THT-HALL-SWITCH"
  AttachedBy = #LCS_Origin
  AttachedTo = PCBA_VSNX_LCDMOUNT_3D_1#LCS_2
  LinkPlacement = pos=(-25.5144,-43.3144,3.74) rot=(0,0,1;0rad)
  LinkedObject = -> <external ../Design/THT-HALL-SWITCH/THT-HALL-SWITCH.FCStd>#Body
  Placement = pos=(-25.5144,-43.3144,3.74) rot=(0,0,1;0rad)
  SolverId = Asm4EE
  expr: Placement = PCBA_VSNX_LCDMOUNT_3D_1.Placement * PCBA_VSNX_LCDMOUNT_LEFT#LCS_2.Placement * AttachmentOffset * THT_HALL_SWITCH#LCS_Origin.Placement ^ -1
FEATURE [Part::FeaturePython] Linear_Body  label="Linear_THT-HALL-SWITCH"  # Draft array (typed FeaturePython)
  ArrayType = Linear Array
  Axis = -> LCS_Origin [X]
  AxisPlacement = pos=(0,0,0) rot=(0.57735,0.57735,0.57735;2.0944rad)
  Count = 4
  Index = 1
  LinearStep = 25.88
  PlacementList = 4 placements: arithmetic series from (-25.5144,-43.3144,3.74) step (25.88,0,2.66454e-15) to (52.1256,-43.3144,3.74)
  Placer = pos=(0,0,77.64) rot=(0,0,1;0rad)
  ScaleList = (4) [(1,1,1),(1,1,1),(1,1,1),(1,1,1)]
  Scaler = 1
  ShowElement = false
  SourceObject = -> Body
  expr: .Placer.Base.z = LinearStep * Index
FEATURE [Part::FeaturePython] Linear_Linear_Body  label="Linear_Linear_THT-HALL-SWITCH"  # Draft array (typed FeaturePython)
  ArrayType = Linear Array
  Axis = -> LCS_Origin [Y]
  AxisPlacement = pos=(0,0,0) rot=(0.57735,0.57735,0.57735;4.18879rad)
  Count = 2
  Index = 1
  LinearStep = 25.88
  PlacementList = 2 placements: [(0,0,0),(8.61977e-15,25.88,-8.61977e-15)]
  Placer = pos=(0,0,25.88) rot=(0,0,1;0rad)
  ScaleList = (2) [(1,1,1),(1,1,1)]
  Scaler = 1
  ShowElement = false
  SourceObject = -> Linear_Body
  expr: .Placer.Base.z = LinearStep * Index
FEATURE [App::Link] PLASTIC_LOW_PROFILE_KEYCAP  label="PLASTIC-LOW-PROFILE-KEYCAP"
  AttachedBy = #LCS_1
  AttachedTo = Body#LCS_1
  AttachmentOffset = pos=(0,0,0) rot=(0,0,1;1.5708rad)
  LinkPlacement = pos=(-38.8144,-38.8144,10.0402) rot=(0,0,-1;3.14159rad)
  LinkedObject = -> <external ../Design/PLASTIC-LOW-PROFILE-KEYCAP/PLASTIC-LOW-PROFILE-KEYCAP_THT.FCStd>#Body
  Placement = pos=(-38.8144,-38.8144,10.0402) rot=(0,0,-1;3.14159rad)
  SolverId = Asm4EE
  expr: Placement = Body.Placement * THT_HALL_SWITCH#LCS_1.Placement * AttachmentOffset * PLASTIC_LOW_PROFILE_KEYCAP_THT#LCS_1.Placement ^ -1
FEATURE [Part::FeaturePython] Linear_PLASTIC_LOW_PROFILE_KEYCAP  label="Linear_PLASTIC-LOW-PROFILE-KEYCAP"  # Draft array (typed FeaturePython)
  ArrayType = Linear Array
  Axis = -> LCS_Origin [X]
  AxisPlacement = pos=(0,0,0) rot=(0.57735,0.57735,0.57735;2.0944rad)
  Count = 4
  Index = 1
  LinearStep = 25.88
  PlacementList = 4 placements: arithmetic series from (-38.8144,-38.8144,10.0402) step (25.88,0,3.55271e-15) to (38.8256,-38.8144,10.0402)
  Placer = pos=(0,0,77.64) rot=(0,0,1;0rad)
  ScaleList = (4) [(1,1,1),(1,1,1),(1,1,1),(1,1,1)]
  Scaler = 1
  ShowElement = false
  SourceObject = -> PLASTIC_LOW_PROFILE_KEYCAP
  expr: .Placer.Base.z = LinearStep * Index
FEATURE [Part::FeaturePython] Linear_Linear_PLASTIC_LOW_PROFILE_KEYCAP  label="Linear_Linear_PLASTIC-LOW-PROFILE-KEYCAP"  # Draft array (typed FeaturePython)
  ArrayType = Linear Array
  Axis = -> LCS_Origin [Y]
  AxisPlacement = pos=(0,0,0) rot=(0.57735,0.57735,0.57735;4.18879rad)
  Count = 2
  Index = 1
  LinearStep = 25.88
  PlacementList = 2 placements: [(0,0,0),(8.61977e-15,25.88,-8.61977e-15)]
  Placer = pos=(0,0,25.88) rot=(0,0,1;0rad)
  ScaleList = (2) [(1,1,1),(1,1,1)]
  Scaler = 1
  ShowElement = false
  SourceObject = -> Linear_PLASTIC_LOW_PROFILE_KEYCAP
  expr: .Placer.Base.z = LinearStep * Index
FEATURE [App::Link] SPACER
  AttachedBy = #LCS_1
  AttachedTo = PCBA_VSNX_3D_1#LCS_3
  AttachmentOffset = pos=(0,0,0) rot=(1,0,0;3.14159rad)
  LinkPlacement = pos=(-26.67,-26.67,1.51) rot=(0,0,-1;3.14159rad)
  LinkedObject = -> <external ../Design/SPACER/SPACER.FCStd>#Body004
  Placement = pos=(-26.67,-26.67,1.51) rot=(0,0,-1;3.14159rad)
  SolverId = Asm4EE
  expr: Placement = PCBA_VSNX_3D_1.Placement * PCBA_VSNX#LCS_3.Placement * AttachmentOffset * SPACER#LCS_1.Placement ^ -1
FEATURE [App::Link] SPACER001
  AttachedBy = #LCS_1
  AttachedTo = PCBA_VSNX_3D_1#LCS_4
  AttachmentOffset = pos=(0,0,0) rot=(1,0,0;3.14159rad)
  LinkPlacement = pos=(26.67,-26.67,1.51) rot=(0,0,-1;3.14159rad)
  LinkedObject = -> <external ../Design/SPACER/SPACER.FCStd>#Body004
  Placement = pos=(26.67,-26.67,1.51) rot=(0,0,-1;3.14159rad)
  SolverId = Asm4EE
  expr: Placement = PCBA_VSNX_3D_1.Placement * PCBA_VSNX#LCS_4.Placement * AttachmentOffset * SPACER#LCS_1.Placement ^ -1
FEATURE [App::Link] SCREW_M1_6x8  label="SCREW-M1.6x8"
  AttachedBy = #LCS_1
  AttachedTo = SPACER#LCS_2
  LinkPlacement = pos=(-26.67,-26.67,3.51) rot=(0,0,-1;3.14159rad)
  LinkedObject = -> <external ../Design/SCREW-M1.6x8/SCREW-M1.6x8.FCStd>#Body
  Placement = pos=(-26.67,-26.67,3.51) rot=(0,0,-1;3.14159rad)
  SolverId = Asm4EE
  expr: Placement = SPACER.Placement * SPACER#LCS_2.Placement * AttachmentOffset * SCREW_M1_6x8#LCS_1.Placement ^ -1
FEATURE [App::Link] SCREW_M1_6x009  label="SCREW-M1.6x009"
  AttachedBy = #LCS_1
  AttachedTo = SPACER001#LCS_2
  LinkPlacement = pos=(26.67,-26.67,3.51) rot=(0,0,-1;3.14159rad)
  LinkedObject = -> <external ../Design/SCREW-M1.6x8/SCREW-M1.6x8.FCStd>#Body
  Placement = pos=(26.67,-26.67,3.51) rot=(0,0,-1;3.14159rad)
  SolverId = Asm4EE
  expr: Placement = SPACER001.Placement * SPACER#LCS_2.Placement * AttachmentOffset * SCREW_M1_6x8#LCS_1.Placement ^ -1
FEATURE [App::Link] PLASTIC_TEK2_KNOB_INTERFACE  label="PLASTIC-TEK2-KNOB-INTERFACE"
  AttachedBy = #LCS_2
  AttachedTo = THT_ENDLESSPOT#LCS_2
  AttachmentOffset = pos=(0,0,0) rot=(-1,0,0;3.14159rad)
  LinkPlacement = pos=(26.67,26.67,22.06) rot=(0,0,1;4.71204rad)
  LinkedObject = -> <external ../Design/PLASTIC-TEK2-KNOB-INTERFACE/PLASTIC-TEK2-KNOB-INTERFACE.FCStd>#Body
  Placement = pos=(26.67,26.67,22.06) rot=(0,0,1;4.71204rad)
  SolverId = Asm4EE
  expr: Placement = THT_ENDLESSPOT.Placement * THT_ENDLESSPOT#LCS_2.Placement * AttachmentOffset * PLASTIC_TEK2_KNOB_INTERFACE#LCS_2.Placement ^ -1
FEATURE [App::Link] KNOB_TEK2  label="KNOB-TEK2"
  AttachedBy = #LCS_1
  AttachedTo = PLASTIC_TEK2_KNOB_INTERFACE#LCS_1
  AttachmentOffset = pos=(0,0,0) rot=(0,0,1;3.14159rad)
  LinkPlacement = pos=(27.4105,26.6719,12.81) rot=(0,0,-1;4.70988rad)
  LinkedObject = -> <external ../Design/KNOB-TEK2/KNOB-TEK2.FCStd>#Body
  Placement = pos=(27.4105,26.6719,12.81) rot=(0,0,-1;4.70988rad)
  SolverId = Asm4EE
  expr: Placement = PLASTIC_TEK2_KNOB_INTERFACE.Placement * PLASTIC_TEK2_KNOB_INTERFACE#LCS_1.Placement * AttachmentOffset * KNOB_TEK2#LCS_1.Placement ^ -1
FEATURE [App::Link] PLASTIC_VSN1_DISPLAY_INTERFACE_merged_left  label="PLASTIC-VSN1-DISPLAY-INTERFACE_merged_left"
  AttachedBy = #LCS_2
  AttachedTo = PCBA_VSNX_LCDMOUNT_3D_1#LCS_1
  AttachmentOffset = pos=(0,0,1.13) rot=(0,0,1;0rad)
  LinkPlacement = pos=(-26.67,26.67,9.905) rot=(0,0,1;0rad)
  LinkedObject = -> <external ../Design/PLASTIC-VSN1-DISPLAY-INTERFACE/PLASTIC-VSN1-DISPLAY-INTERFACE_merged_left.FCStd>#Body
  Placement = pos=(-26.67,26.67,9.905) rot=(0,0,1;0rad)
  SolverId = Asm4EE
  expr: Placement = PCBA_VSNX_LCDMOUNT_3D_1.Placement * PCBA_VSNX_LCDMOUNT_LEFT#LCS_1.Placement * AttachmentOffset * PLASTIC_VSN1_DISPLAY_INTERFACE_merged_left#LCS_2.Placement ^ -1
FEATURE [App::Part] Assembly
  AssemblyType = Part::Link
  Group = -> [LCS_Origin,Constraints,Variables,Configurations,PCBA_VSNX_3D_1,PCBA_VSNX_SPACER_3D_1,PCBA_VSNX_SPACER_3D_002,PCBA_VSNX_LCDMOUNT_3D_1,THT_ENDLESSPOT,SCREW_M1_6x5_C,SCREW_M1_6x5_C001,SCREW_M1_6x5_C002,SCREW_M1_6x5_C003,SCREW_M1_6x5_C004,SCREW_M1_6x5_C005,SCREW_M1_6x5_C006,SCREW_M1_6x5_C007,PLASTIC_VSN1_DISPLAY_INTERFACE,PLASTIC_VSN1_BUTTON,Body,Linear_Body,Linear_Linear_Body,+10 more]
  Origin = -> Origin
  Type = Assembly
